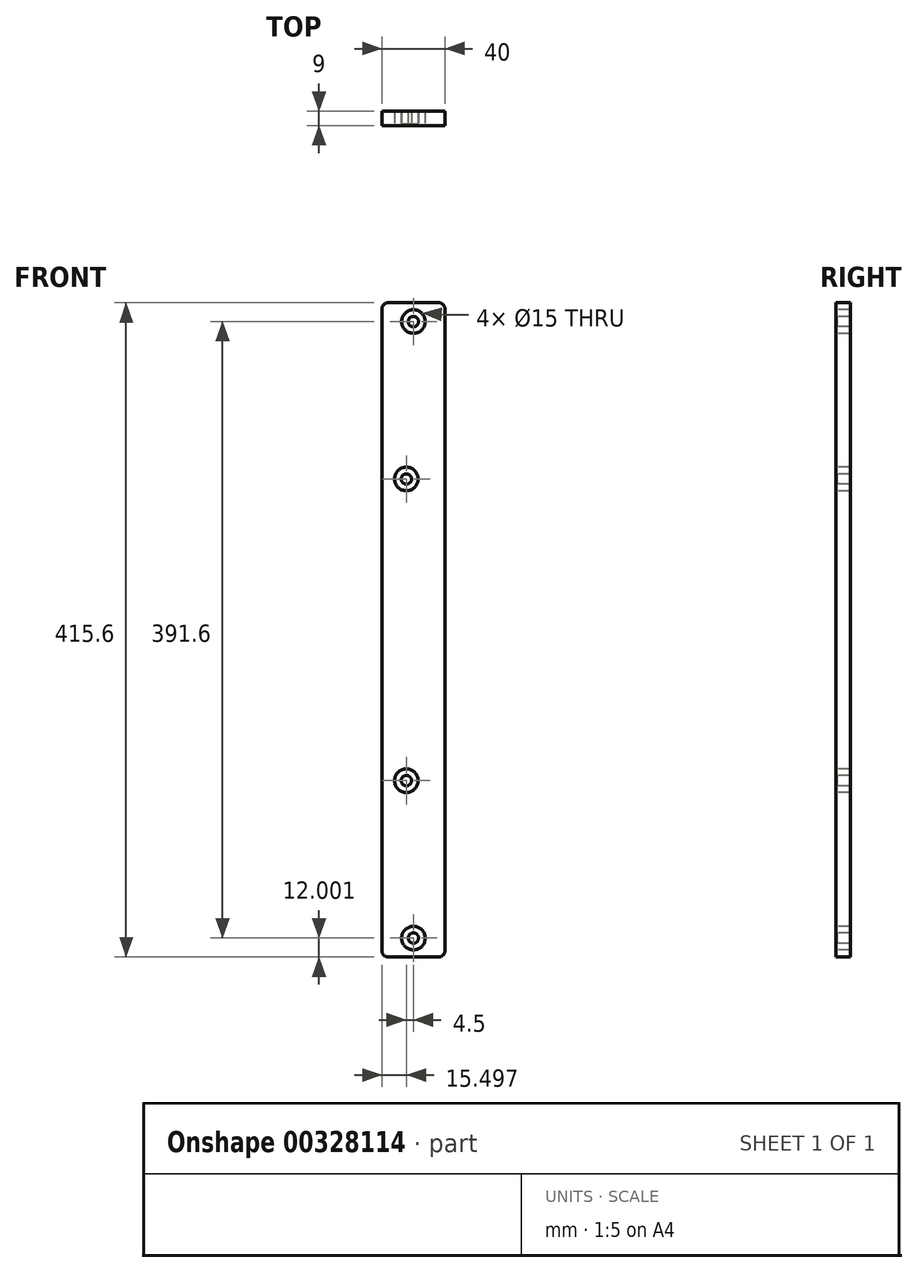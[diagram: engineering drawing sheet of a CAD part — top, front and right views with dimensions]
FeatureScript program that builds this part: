
annotation { "Feature Type Name" : "Feature", "Feature Type Description" : "" }
export const myFeature = defineFeature(function(context is Context, id is Id, definition is map)
    precondition{}
    {
        {
            var Q0;
            Q0=qCreatedBy(makeId("Front.planeOp"),FACE);
            var sketch = newSketch(context, id + "F0", { "sketchPlane" : qUnion([Q0])});
            skLineSegment(sketch, "E0", {"start": v(-52.86, -164.97) * mm, "end": v(-20.86, -164.97) * mm});
            skArc(sketch, "E1", {"start": v(-20.86, -164.97) * mm, "mid": v(-18.04, -163.8) * mm, "end": v(-16.86, -160.97) * mm});
            skLineSegment(sketch, "E2", {"start": v(-16.86, -160.97) * mm, "end": v(-16.86, 246.63) * mm});
            skArc(sketch, "E3", {"start": v(-16.86, 246.63) * mm, "mid": v(-18.04, 249.46) * mm, "end": v(-20.86, 250.63) * mm});
            skLineSegment(sketch, "E4", {"start": v(-20.86, 250.63) * mm, "end": v(-52.86, 250.63) * mm});
            skArc(sketch, "E5", {"start": v(-52.86, 250.63) * mm, "mid": v(-55.7, 249.46) * mm, "end": v(-56.86, 246.63) * mm});
            skLineSegment(sketch, "E6", {"start": v(-56.86, 246.63) * mm, "end": v(-56.86, -160.97) * mm});
            skArc(sketch, "E7", {"start": v(-56.86, -160.97) * mm, "mid": v(-55.7, -163.8) * mm, "end": v(-52.86, -164.97) * mm});
            skCircle(sketch, "E8", {"center": v(-36.86, 238.63) * mm, "radius": 3.3 * mm});
            skCircle(sketch, "E9", {"center": v(-41.36, 138.63) * mm, "radius": 3.3 * mm});
            skCircle(sketch, "E10", {"center": v(-41.36, -52.97) * mm, "radius": 3.3 * mm});
            skCircle(sketch, "E11", {"center": v(-36.86, -152.97) * mm, "radius": 3.3 * mm});
            skCircle(sketch, "E12", {"center": v(-36.86, -152.97) * mm, "radius": 7.5 * mm});
            skCircle(sketch, "E13", {"center": v(-41.36, -52.97) * mm, "radius": 7.5 * mm});
            skCircle(sketch, "E14", {"center": v(-36.86, 238.63) * mm, "radius": 7.5 * mm});
            skCircle(sketch, "E15", {"center": v(-41.36, 138.63) * mm, "radius": 7.5 * mm});
            skArc(sketch, "E16", {"start": v(-6.14, 246.23) * mm, "mid": v(-10.25, 256.13) * mm, "end": v(-20.14, 260.23) * mm});
            skLineSegment(sketch, "E17", {"start": v(-20.14, 260.23) * mm, "end": v(-52.14, 260.23) * mm});
            skArc(sketch, "E18", {"start": v(-52.14, 260.23) * mm, "mid": v(-62.04, 256.13) * mm, "end": v(-66.14, 246.23) * mm});
            skLineSegment(sketch, "E19", {"start": v(-66.14, 246.23) * mm, "end": v(-66.14, -161.37) * mm});
            skArc(sketch, "E20", {"start": v(-66.14, -161.37) * mm, "mid": v(-62.04, -171.27) * mm, "end": v(-52.14, -175.37) * mm});
            skLineSegment(sketch, "E21", {"start": v(-52.14, -175.37) * mm, "end": v(-20.14, -175.37) * mm});
            skArc(sketch, "E22", {"start": v(-20.14, -175.37) * mm, "mid": v(-10.25, -171.27) * mm, "end": v(-6.14, -161.37) * mm});
            skLineSegment(sketch, "E23", {"start": v(-6.14, -161.37) * mm, "end": v(-6.14, 246.23) * mm});
            skSolve(sketch);
        }
        {
            var Q0;
            Q0=makeQuery(id+"F0.imprint","IMPRINT",FACE,{"disambiguationData":[TD([[makeQuery(id+"F0.imprint","IMPRINT",EDGE,{"derivedFrom":sQuery(id+"F0.wireOp",EDGE,"E0")}),1.0]])]});
            var Q1;
            Q1=makeQuery(id+"F0.imprint","IMPRINT",FACE,{"disambiguationData":[TD([[makeQuery(id+"F0.imprint","IMPRINT",EDGE,{"derivedFrom":sQuery(id+"F0.wireOp",EDGE,"E8")}),1.0]])]});
            var Q2;
            Q2=makeQuery(id+"F0.imprint","IMPRINT",FACE,{"disambiguationData":[TD([[makeQuery(id+"F0.imprint","IMPRINT",EDGE,{"derivedFrom":sQuery(id+"F0.wireOp",EDGE,"E9")}),1.0]])]});
            var Q3;
            Q3=makeQuery(id+"F0.imprint","IMPRINT",FACE,{"disambiguationData":[TD([[makeQuery(id+"F0.imprint","IMPRINT",EDGE,{"derivedFrom":sQuery(id+"F0.wireOp",EDGE,"E10")}),1.0]])]});
            var Q4;
            Q4=makeQuery(id+"F0.imprint","IMPRINT",FACE,{"disambiguationData":[TD([[makeQuery(id+"F0.imprint","IMPRINT",EDGE,{"derivedFrom":sQuery(id+"F0.wireOp",EDGE,"E11")}),1.0]])]});
            extrude(context, id + "F1", {"entities" : qUnion([Q0, Q1, Q2, Q3, Q4]), "oppositeDirection" : true, "depth" : 18 * mm});
        }
        {
            var Q0;
            Q0=makeQuery(id+"F0.imprint","IMPRINT",FACE,{"disambiguationData":[TD([[makeQuery(id+"F0.imprint","IMPRINT",EDGE,{"derivedFrom":sQuery(id+"F0.wireOp",EDGE,"E0")}),-1.0]])]});
            var Q1;
            Q1=makeQuery(id+"F0.imprint","IMPRINT",FACE,{"disambiguationData":[TD([[makeQuery(id+"F0.imprint","IMPRINT",EDGE,{"derivedFrom":sQuery(id+"F0.wireOp",EDGE,"E8")}),-1.0]])]});
            var Q2;
            Q2=makeQuery(id+"F0.imprint","IMPRINT",FACE,{"disambiguationData":[TD([[makeQuery(id+"F0.imprint","IMPRINT",EDGE,{"derivedFrom":sQuery(id+"F0.wireOp",EDGE,"E9")}),1.0]])]});
            var Q3;
            Q3=makeQuery(id+"F0.imprint","IMPRINT",FACE,{"disambiguationData":[TD([[makeQuery(id+"F0.imprint","IMPRINT",EDGE,{"derivedFrom":sQuery(id+"F0.wireOp",EDGE,"E9")}),-1.0]])]});
            var Q4;
            Q4=makeQuery(id+"F0.imprint","IMPRINT",FACE,{"disambiguationData":[TD([[makeQuery(id+"F0.imprint","IMPRINT",EDGE,{"derivedFrom":sQuery(id+"F0.wireOp",EDGE,"E10")}),1.0]])]});
            var Q5;
            Q5=makeQuery(id+"F0.imprint","IMPRINT",FACE,{"disambiguationData":[TD([[makeQuery(id+"F0.imprint","IMPRINT",EDGE,{"derivedFrom":sQuery(id+"F0.wireOp",EDGE,"E10")}),-1.0]])]});
            var Q6;
            Q6=makeQuery(id+"F0.imprint","IMPRINT",FACE,{"disambiguationData":[TD([[makeQuery(id+"F0.imprint","IMPRINT",EDGE,{"derivedFrom":sQuery(id+"F0.wireOp",EDGE,"E8")}),1.0]])]});
            var Q7;
            Q7=makeQuery(id+"F0.imprint","IMPRINT",FACE,{"disambiguationData":[TD([[makeQuery(id+"F0.imprint","IMPRINT",EDGE,{"derivedFrom":sQuery(id+"F0.wireOp",EDGE,"E0")}),1.0]])]});
            var Q8;
            Q8=makeQuery(id+"F0.imprint","IMPRINT",FACE,{"disambiguationData":[TD([[makeQuery(id+"F0.imprint","IMPRINT",EDGE,{"derivedFrom":sQuery(id+"F0.wireOp",EDGE,"E11")}),1.0]])]});
            var Q9;
            Q9=makeQuery(id+"F0.imprint","IMPRINT",FACE,{"disambiguationData":[TD([[makeQuery(id+"F0.imprint","IMPRINT",EDGE,{"derivedFrom":sQuery(id+"F0.wireOp",EDGE,"E11")}),-1.0]])]});
            extrude(context, id + "F2", {"entities" : qUnion([Q0, Q1, Q2, Q3, Q4, Q5, Q6, Q7, Q8, Q9]), "operationType" : NewBodyOperationType.REMOVE, "oppositeDirection" : true, "depth" : 9 * mm});
        }
        {
            var Q0;
            Q0=makeQuery(id+"F0.imprint","IMPRINT",FACE,{"disambiguationData":[TD([[makeQuery(id+"F0.imprint","IMPRINT",EDGE,{"derivedFrom":sQuery(id+"F0.wireOp",EDGE,"E8")}),1.0]])]});
            var Q1;
            Q1=makeQuery(id+"F0.imprint","IMPRINT",FACE,{"disambiguationData":[TD([[makeQuery(id+"F0.imprint","IMPRINT",EDGE,{"derivedFrom":sQuery(id+"F0.wireOp",EDGE,"E9")}),1.0]])]});
            var Q2;
            Q2=makeQuery(id+"F0.imprint","IMPRINT",FACE,{"disambiguationData":[TD([[makeQuery(id+"F0.imprint","IMPRINT",EDGE,{"derivedFrom":sQuery(id+"F0.wireOp",EDGE,"E10")}),1.0]])]});
            var Q3;
            Q3=makeQuery(id+"F0.imprint","IMPRINT",FACE,{"disambiguationData":[TD([[makeQuery(id+"F0.imprint","IMPRINT",EDGE,{"derivedFrom":sQuery(id+"F0.wireOp",EDGE,"E11")}),1.0]])]});
            extrude(context, id + "F3", {"entities" : qUnion([Q0, Q1, Q2, Q3]), "operationType" : NewBodyOperationType.REMOVE, "oppositeDirection" : true, "depth" : 10 * mm});
        }
    });
